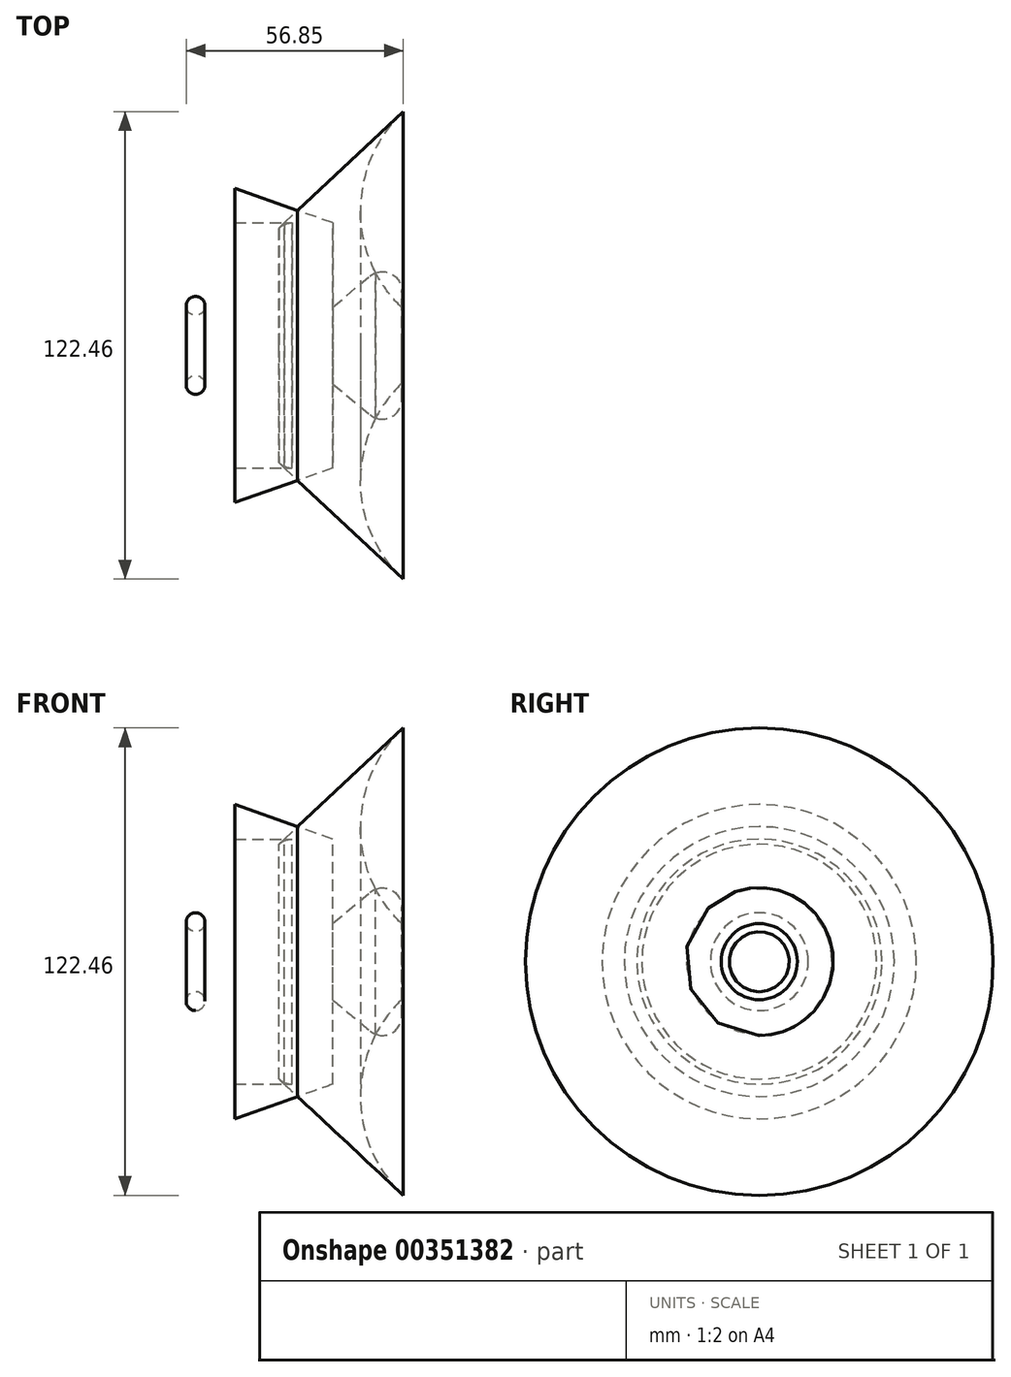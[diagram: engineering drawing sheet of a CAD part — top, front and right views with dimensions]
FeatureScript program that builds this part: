
annotation { "Feature Type Name" : "Feature", "Feature Type Description" : "" }
export const myFeature = defineFeature(function(context is Context, id is Id, definition is map)
    precondition{}
    {
        {
            var Q0;
            Q0=qCreatedBy(makeId("Front.planeOp"),FACE);
            var sketch = newSketch(context, id + "F0", { "sketchPlane" : qUnion([Q0])});
            skLineSegment(sketch, "E0", {"start": v(62.62, 0) * mm, "end": v(0, 0) * mm});
            skLineSegment(sketch, "E1", {"start": v(5.85, 30.74) * mm, "end": v(38.44, 61.23) * mm});
            skLineSegment(sketch, "E2", {"start": v(-5.72, 32.1) * mm, "end": v(9.27, 32.1) * mm});
            skLineSegment(sketch, "E3", {"start": v(-5.72, 32.1) * mm, "end": v(-5.72, 41.16) * mm});
            skLineSegment(sketch, "E4", {"start": v(-5.72, 41.16) * mm, "end": v(20.05, 32.1) * mm});
            skLineSegment(sketch, "E5", {"start": v(20.05, 32.1) * mm, "end": v(20.05, 10.1) * mm});
            skLineSegment(sketch, "E6", {"start": v(20.05, 10.1) * mm, "end": v(29.8, 18.2) * mm});
            skLineSegment(sketch, "E7", {"start": v(38, 14.35) * mm, "end": v(38, 0) * mm});
            skLineSegment(sketch, "E8", {"start": v(38, 0) * mm, "end": v(0, 0) * mm});
            skLineSegment(sketch, "E9", {"start": v(70.05, 0) * mm, "end": v(-65.7, 0) * mm});
            skPoint(sketch, "E10.visualSharp", {"position": v(7.3, 32.1) * mm});
            skArc(sketch, "E10.filletArc", {"start": v(9.27, 32.1) * mm, "mid": v(7.43, 31.74) * mm, "end": v(5.85, 30.74) * mm});
            skPoint(sketch, "E11.visualSharp", {"position": v(38, 25) * mm});
            skArc(sketch, "E11.filletArc", {"start": v(38, 14.35) * mm, "mid": v(35.12, 18.87) * mm, "end": v(29.8, 18.2) * mm});
            skPoint(sketch, "E12.visualSharp", {"position": v(-27, 0) * mm});
            skArc(sketch, "E12.filletArc", {"start": v(38.44, 61.23) * mm, "mid": v(29.7, 22.4) * mm, "end": v(62.62, 0) * mm});
            skCircle(sketch, "E13", {"center": v(-15.94, 10.35) * mm, "radius": 2.47 * mm});
            skSolve(sketch);
        }
        {
            var Q0;
            Q0 = qSketchRegion(id + "F0", true);
            var Q1;
            Q1=sQuery(id+"F0.wireOp",EDGE,"E9");
            revolve(context, id + "F1", {"entities" : qUnion([Q0]), "axis" : qUnion([Q1]), "revolveType" : RevolveType.FULL});
        }
    });
